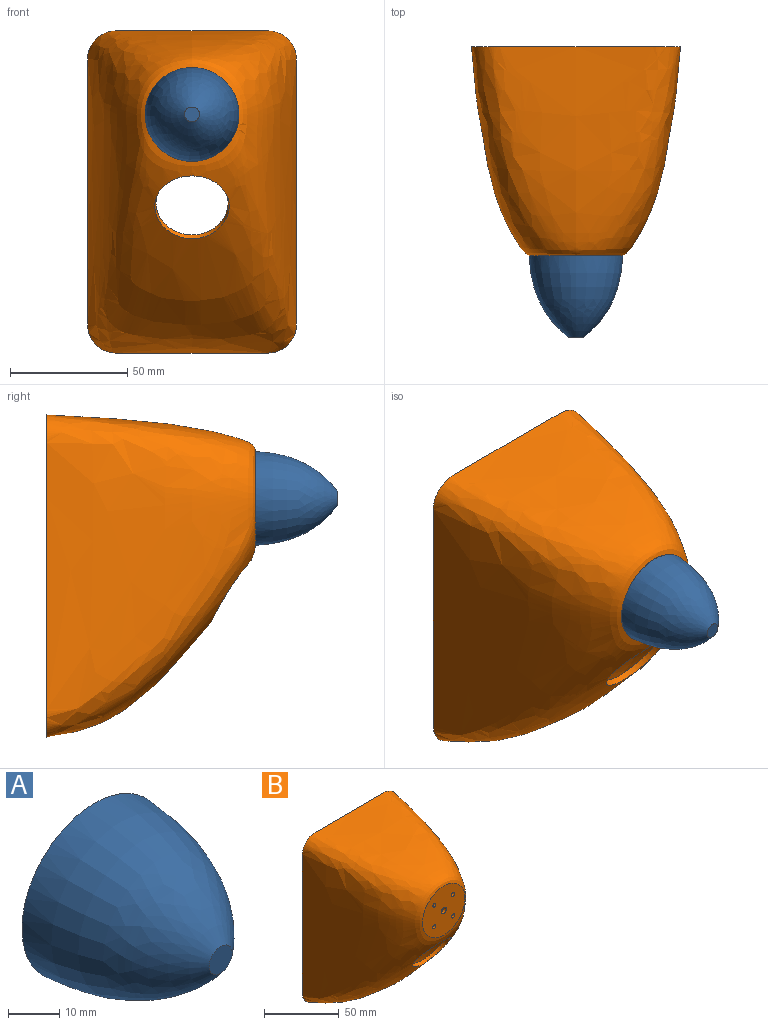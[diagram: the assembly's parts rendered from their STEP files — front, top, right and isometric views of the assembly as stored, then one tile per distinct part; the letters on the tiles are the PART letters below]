
ASSEMBLY  parts=2 mates=1
PART A: 3 faces, bbox 40x34.8x40 mm
  f0: plane 40x40mm, normal (0,1,0), area 1256.6mm2, adj f1
  f1: revolved ~40x40mm, area 3588.1mm2, adj f0,f2
  f2: plane 6.35x6.35mm, normal (0,-1,0), area 31.7mm2, adj f1
PART B: 16 faces, bbox 94.7x95x142.9 mm
  f0: plane 142.81x94.55mm, normal (0,1,0), area 1091.5mm2, adj f2,f7
  f1: plane 41.21x41.21mm, normal (0,-1,0), area 1207.4mm2, adj f2,f10,f11,f12,f13,f14
  f2: bspline ~137.16x88.9mm, area 31079.8mm2, adj f0,f1,f15
  f3: offset ~23.13x15.36mm, area 25.5mm2, adj f4,f7,f8,f9
  f4: bspline ~25.19x5.13mm, area 49.7mm2, adj f3,f5,f7,f8
  f5: offset ~45.12x18.96mm, area 125.1mm2, adj f4,f6,f7,f8
  f6: bspline ~25.19x5.13mm, area 50.3mm2, adj f5,f7,f8,f9
  f7: offset ~142.36x94.1mm, area 28544.2mm2, adj f0,f3,f4,f5,f6,f9,f15
  f8: plane 40.68x39.51mm, normal (0,1,0), area 1131.7mm2, adj f3,f4,f5,f6,f9,f10,f11,f12
  f9: offset ~22.99x15.2mm, area 25.5mm2, adj f3,f6,f7,f8
  f10: cylinder r=1.5mm len=3mm, axis (0,-1,0), area 23.9mm2, adj f1,f8
  f11: cylinder r=2.5mm len=5mm, axis (0,-1,0), area 39.9mm2, adj f1,f8
  f12: cylinder r=1.5mm len=3mm, axis (0,-1,0), area 23.9mm2, adj f1,f8
  f13: cylinder r=1.5mm len=3mm, axis (0,-1,0), area 23.9mm2, adj f1,f8
  f14: cylinder r=1.5mm len=3mm, axis (0,-1,0), area 23.9mm2, adj f1,f8
  f15: sphere r=15.94mm, area 251.3mm2, adj f2,f7
PLACE A t=(-22.31,46.84,12.41)mm
PLACE B t=(-22.31,36.68,12.41)mm
MATE fastened B.f11 <-> A.f0  axis (0,-1,0) through (-22.31,36.68,12.41)mm
